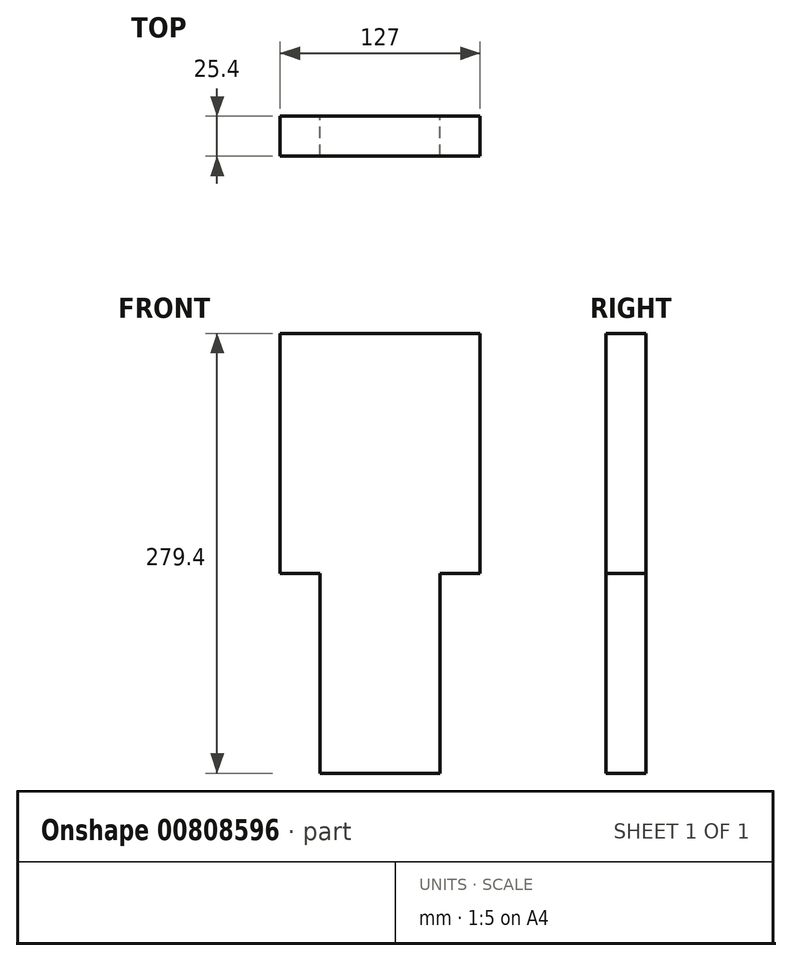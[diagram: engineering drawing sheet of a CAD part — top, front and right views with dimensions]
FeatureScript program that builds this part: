
annotation { "Feature Type Name" : "Feature", "Feature Type Description" : "" }
export const myFeature = defineFeature(function(context is Context, id is Id, definition is map)
    precondition{}
    {
        {
            var Q0;
            Q0=qCreatedBy(makeId("Front.planeOp"),FACE);
            var sketch = newSketch(context, id + "F0", { "sketchPlane" : qUnion([Q0])});
            skLineSegment(sketch, "E0.bottom", {"start": v(14.58, 134.6) * mm, "end": v(39.98, 134.6) * mm});
            skLineSegment(sketch, "E0.top", {"start": v(14.58, -17.8) * mm, "end": v(39.98, -17.8) * mm});
            skLineSegment(sketch, "E0.left", {"start": v(14.58, 134.6) * mm, "end": v(14.58, -17.8) * mm});
            skLineSegment(sketch, "E0.right", {"start": v(39.98, 134.6) * mm, "end": v(39.98, -17.8) * mm});
            skLineSegment(sketch, "E1", {"start": v(39.98, 134.6) * mm, "end": v(116.18, 134.6) * mm});
            skLineSegment(sketch, "E2", {"start": v(116.18, 134.6) * mm, "end": v(116.18, -17.8) * mm});
            skLineSegment(sketch, "E3", {"start": v(116.18, -17.8) * mm, "end": v(39.98, -17.8) * mm});
            skLineSegment(sketch, "E4", {"start": v(116.18, 134.6) * mm, "end": v(141.58, 134.6) * mm});
            skLineSegment(sketch, "E5", {"start": v(141.58, 134.6) * mm, "end": v(141.58, -17.8) * mm});
            skLineSegment(sketch, "E6", {"start": v(141.58, -17.8) * mm, "end": v(116.18, -17.8) * mm});
            skLineSegment(sketch, "E7", {"start": v(39.98, -17.8) * mm, "end": v(39.98, -144.8) * mm});
            skLineSegment(sketch, "E8", {"start": v(39.98, -144.8) * mm, "end": v(116.18, -144.8) * mm});
            skLineSegment(sketch, "E9", {"start": v(116.18, -144.8) * mm, "end": v(116.18, -17.8) * mm});
            skSolve(sketch);
        }
        {
            var Q0;
            Q0 = qSketchRegion(id + "F0", true);
            extrude(context, id + "F1", {"entities" : qUnion([Q0]), "depth" : 25.4 * mm, "offsetDistance" : 25.4 * mm});
        }
    });
